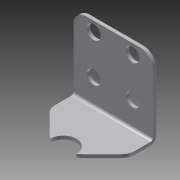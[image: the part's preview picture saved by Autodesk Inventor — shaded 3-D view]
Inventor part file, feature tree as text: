
AUTODESK INVENTOR PART (.ipt)
format: ipt  version: 2014 SP1 (Build 180222100, 222)  size: 232,448 bytes
history: native  units: in
note: dims shown in document units (in); Inventor stores cm internally (conversion verified against a paired STEP export)
features: other x4, sketch x3, sheet_metal_op x2, chamfer x2, extrude x1, reference x1
ambient origin geometry x8: Origin, YZ Plane, XZ Plane, XY Plane, X Axis, Y Axis, Z Axis, Center Point
bodies: Solid1 (feature_tree)
feature tree (13):
  sketch  "Sketch1"  dims[d0=1.5339in d3=0.266in d4=0.266in]
  sheet_metal_op  "Face1"
  sheet_metal_op  "Fold1"
  chamfer  "Corner Round1"
  extrude  "Extrusion1"  Depth=1.5339in
  other  "Corner Chamfer1"
  chamfer  "Corner Round3"
  other  "Plate1"
  sketch  "Sketch2"  dims[d7=1.5in]
  sketch  "Sketch3"  dims[d8=1.5in d9=0.0625in d10=0.0625in d11=0.0312in d12=0.125in d13=0.0625in d14=90.0deg d15=0.05in d22=0.75in d26=0.5in d28=0.266in d29=1.0in d30=0.392in d31=0.7874in d33=0.75in d34=0.7874in d36=0.75in d39=0.25in d40=0.7874in d42=0.75in d43=0.7874in d45=0.75in d48=0.266in d49=0.55in d50=0.0625in d51=0.0in d52=1.0in d53=0.0in d55=0.5in d56=0.25in d57=45.0deg d58=0.25in]
  reference  "Reference1"
  other  "Cut1"
  other  "Definition1"
